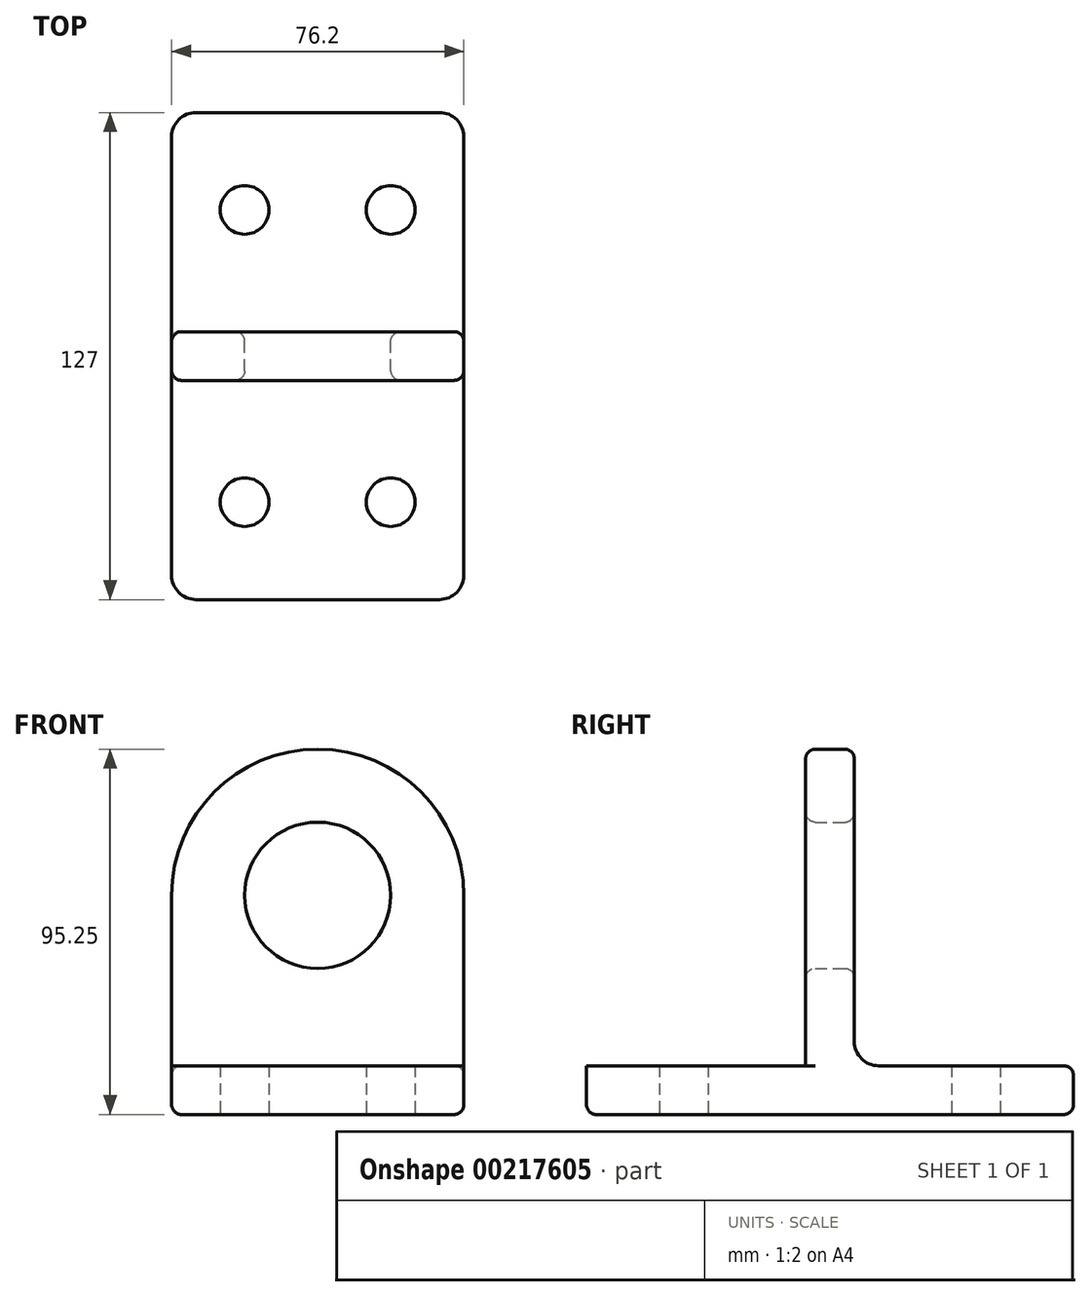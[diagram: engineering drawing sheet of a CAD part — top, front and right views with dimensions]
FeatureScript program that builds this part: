
annotation { "Feature Type Name" : "Feature", "Feature Type Description" : "" }
export const myFeature = defineFeature(function(context is Context, id is Id, definition is map)
    precondition{}
    {
        {
            var Q0;
            Q0=qCreatedBy(makeId("Front.planeOp"),FACE);
            var sketch = newSketch(context, id + "F0", { "sketchPlane" : qUnion([Q0])});
            skCircle(sketch, "E0", {"center": v(0, 0) * mm, "radius": 19.05 * mm});
            skCircle(sketch, "E1", {"center": v(0, 0) * mm, "radius": 38.1 * mm});
            skLineSegment(sketch, "E2", {"start": v(-38.1, 0) * mm, "end": v(-38.1, -44.45) * mm});
            skLineSegment(sketch, "E3", {"start": v(-38.1, -44.45) * mm, "end": v(38.1, -44.45) * mm});
            skLineSegment(sketch, "E4", {"start": v(38.1, -44.45) * mm, "end": v(38.1, 0) * mm});
            skLineSegment(sketch, "E5", {"start": v(-38.1, -44.45) * mm, "end": v(-38.1, -57.15) * mm});
            skLineSegment(sketch, "E6", {"start": v(-38.1, -57.15) * mm, "end": v(38.1, -57.15) * mm});
            skLineSegment(sketch, "E7", {"start": v(38.1, -57.15) * mm, "end": v(38.1, -44.45) * mm});
            skSolve(sketch);
        }
        {
            var Q0;
            Q0=makeQuery(id+"F0.imprint","IMPRINT",FACE,{"disambiguationData":[TD([[makeQuery(id+"F0.imprint","IMPRINT",EDGE,{"derivedFrom":sQuery(id+"F0.wireOp",EDGE,"E3")}),-1.0]])]});
            extrude(context, id + "F1", {"entities" : qUnion([Q0]), "endBound" : BoundingType.SYMMETRIC, "depth" : 127 * mm});
        }
        {
            var Q0;
            Q0=makeQuery(id+"F0.imprint","IMPRINT",FACE,{"disambiguationData":[TD([[makeQuery(id+"F0.imprint","IMPRINT",EDGE,{"derivedFrom":sQuery(id+"F0.wireOp",EDGE,"E0")}),-1.0]])]});
            var Q1;
            {var subQ0=sQuery(id+"F0.wireOp",EDGE,"E2");Q1=makeQuery(id+"F0.imprint","IMPRINT",FACE,{"disambiguationData":[TD([[makeQuery(id+"F0.imprint","IMPRINT",EDGE,{"derivedFrom":subQ0}),1.0]])]});}
            extrude(context, id + "F2", {"entities" : qUnion([Q0, Q1]), "operationType" : NewBodyOperationType.ADD, "endBound" : BoundingType.SYMMETRIC, "depth" : 12.7 * mm});
        }
        {
            var Q0;
            Q0=makeQuery(id+"F1.opExtrude","SWEPT_FACE",FACE,{"disambiguationData":[OSD([sQuery(id+"F0.wireOp",EDGE,"E6")])]});
            var sketch = newSketch(context, id + "F3", { "sketchPlane" : qUnion([Q0])});
            skPoint(sketch, "E8.middle", {"position": v(0, 0) * mm});
            skCircle(sketch, "E9", {"center": v(19.05, 38.1) * mm, "radius": 6.35 * mm});
            skCircle(sketch, "E10", {"center": v(-19.05, 38.1) * mm, "radius": 6.35 * mm});
            skCircle(sketch, "E11", {"center": v(-19.05, -38.1) * mm, "radius": 6.35 * mm});
            skCircle(sketch, "E12", {"center": v(19.05, -38.1) * mm, "radius": 6.35 * mm});
            skSolve(sketch);
        }
        {
            var Q0;
            Q0 = qSketchRegion(id + "F3", true);
            extrude(context, id + "F4", {"entities" : qUnion([Q0]), "operationType" : NewBodyOperationType.REMOVE, "endBound" : BoundingType.THROUGH_ALL, "oppositeDirection" : true, "depth" : 25.4 * mm});
        }
        {
            var Q0;
            Q0=makeQuery(id+"F2.opExtrude","CAP_EDGE",EDGE,{"disambiguationData":[OSD([sQuery(id+"F0.wireOp",EDGE,"E3")])],"isStart":false});
            var Q1;
            Q1=makeQuery(id+"F1.opExtrude","CAP_EDGE",EDGE,{"disambiguationData":[OSD([sQuery(id+"F0.wireOp",EDGE,"E5")])],"isStart":false});
            var Q2;
            Q2=makeQuery(id+"F1.opExtrude","CAP_EDGE",EDGE,{"disambiguationData":[OSD([sQuery(id+"F0.wireOp",EDGE,"E7")])],"isStart":false});
            var Q3;
            Q3=makeQuery(id+"F1.opExtrude","CAP_EDGE",EDGE,{"disambiguationData":[OSD([sQuery(id+"F0.wireOp",EDGE,"E7")])],"isStart":true});
            var Q4;
            Q4=makeQuery(id+"F2.opExtrude","CAP_EDGE",EDGE,{"disambiguationData":[OSD([sQuery(id+"F0.wireOp",EDGE,"E3")])],"isStart":true});
            var Q5;
            Q5=makeQuery(id+"F1.opExtrude","CAP_EDGE",EDGE,{"disambiguationData":[OSD([sQuery(id+"F0.wireOp",EDGE,"E5")])],"isStart":true});
            fillet(context, id + "F5", {"entities" : qUnion([Q0, Q1, Q2, Q3, Q4, Q5]), "radius" : 6.35 * mm, "tangentPropagation" : true, "allowEdgeOverflow" : false});
        }
        {
            var Q0;
            Q0=makeQuery(id+"F2.opExtrude","CAP_EDGE",EDGE,{"disambiguationData":[OSD([sQuery(id+"F0.wireOp",EDGE,"E4")])],"isStart":false});
            var Q1;
            Q1=makeQuery(id+"F2.opExtrude","CAP_EDGE",EDGE,{"disambiguationData":[OSD([sQuery(id+"F0.wireOp",EDGE,"E4")])],"isStart":true});
            var Q2;
            Q2=makeQuery(id+"F1.opExtrude","SWEPT_EDGE",EDGE,{"disambiguationData":[OSD([sQuery(id+"F0.wireOp",EDGE,"E6"),sQuery(id+"F0.wireOp",EDGE,"E7")])]});
            var Q3;
            Q3=makeQuery(id+"F2.opExtrude","CAP_EDGE",EDGE,{"disambiguationData":[OSD([sQuery(id+"F0.wireOp",EDGE,"E0")])],"isStart":false});
            var Q4;
            Q4=makeQuery(id+"F2.opExtrude","CAP_EDGE",EDGE,{"disambiguationData":[OSD([sQuery(id+"F0.wireOp",EDGE,"E0")])],"isStart":true});
            fillet(context, id + "F6", {"entities" : qUnion([Q0, Q1, Q2, Q3, Q4]), "radius" : 2.54 * mm, "tangentPropagation" : true, "allowEdgeOverflow" : false});
        }
    });
